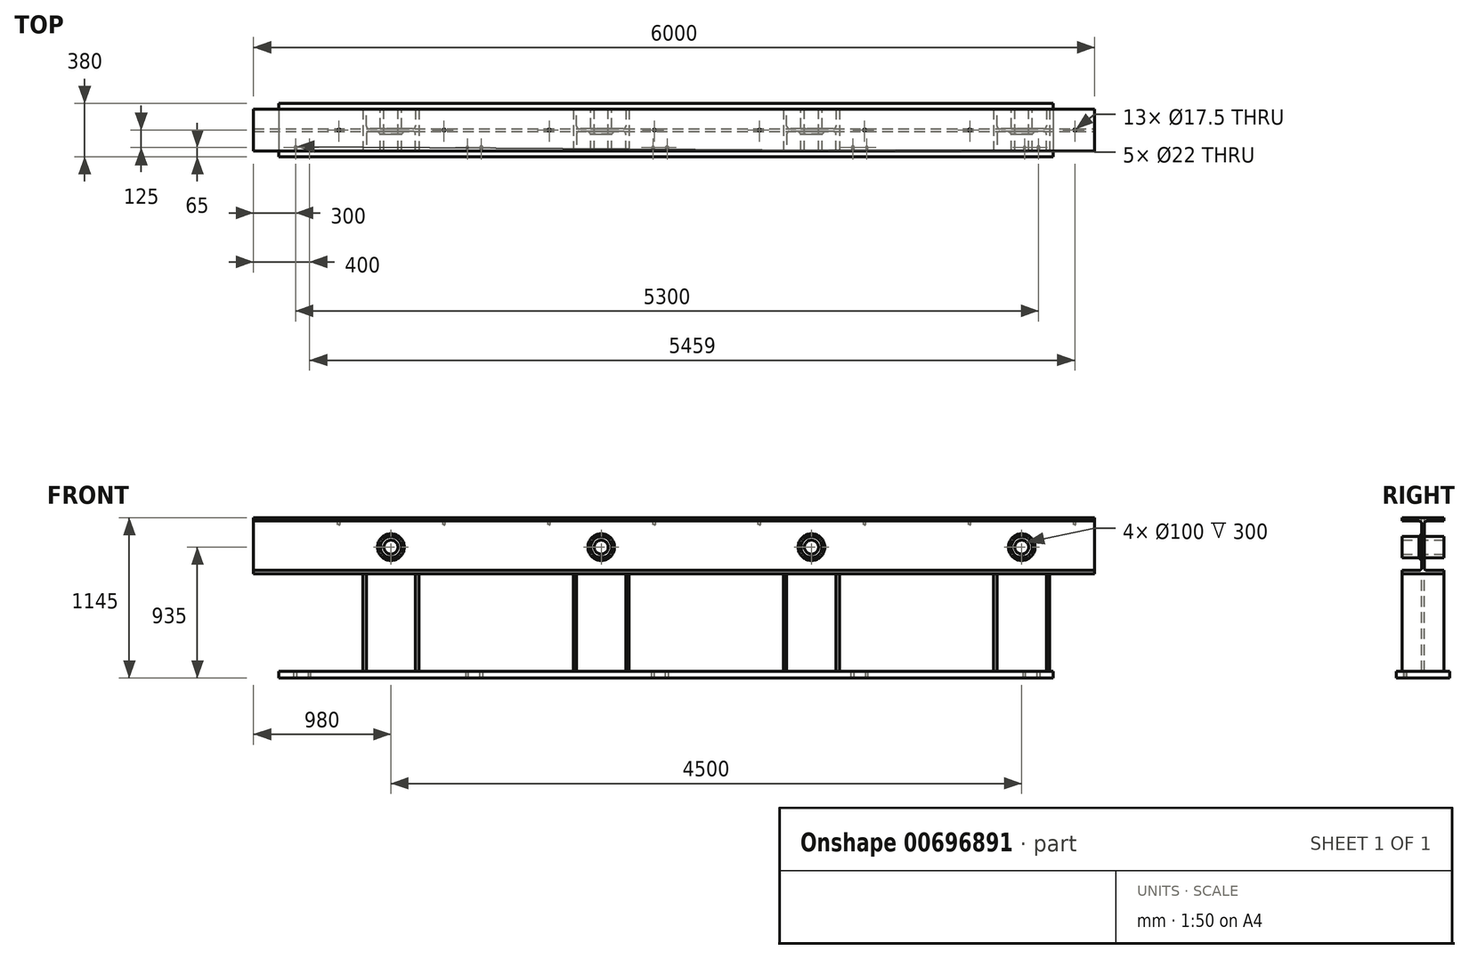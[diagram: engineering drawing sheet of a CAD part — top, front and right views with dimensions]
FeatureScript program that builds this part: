
annotation { "Feature Type Name" : "Feature", "Feature Type Description" : "" }
export const myFeature = defineFeature(function(context is Context, id is Id, definition is map)
    precondition{}
    {
        {
            var Q0;
            Q0=qCreatedBy(makeId("Right.planeOp"),FACE);
            var sketch = newSketch(context, id + "F0", { "sketchPlane" : qUnion([Q0])});
            skLineSegment(sketch, "E0", {"start": v(0, 400) * mm, "end": v(0, 0) * mm, "construction": true});
            skLineSegment(sketch, "E1", {"start": v(0, 0) * mm, "end": v(150, 0) * mm});
            skLineSegment(sketch, "E2", {"start": v(150, 0) * mm, "end": v(150, 24) * mm});
            skLineSegment(sketch, "E3", {"start": v(150, 24) * mm, "end": v(28.5, 24) * mm});
            skLineSegment(sketch, "E4", {"start": v(9.5, 43) * mm, "end": v(9.5, 357) * mm});
            skLineSegment(sketch, "E5", {"start": v(28.5, 376) * mm, "end": v(150, 376) * mm});
            skLineSegment(sketch, "E6", {"start": v(150, 376) * mm, "end": v(150, 400) * mm});
            skLineSegment(sketch, "E7", {"start": v(150, 400) * mm, "end": v(0, 400) * mm});
            skLineSegment(sketch, "E8.MirrorCS", {"start": v(-150, 0) * mm, "end": v(-150, 24) * mm});
            skLineSegment(sketch, "E9.MirrorCS", {"start": v(-150, 376) * mm, "end": v(-150, 400) * mm});
            skLineSegment(sketch, "E10.MirrorCS", {"start": v(-9.5, 43) * mm, "end": v(-9.5, 357) * mm});
            skLineSegment(sketch, "E11.MirrorCS", {"start": v(-150, 24) * mm, "end": v(-28.5, 24) * mm});
            skLineSegment(sketch, "E12.MirrorCS", {"start": v(-150, 400) * mm, "end": v(0, 400) * mm});
            skLineSegment(sketch, "E13.MirrorCS", {"start": v(0, 0) * mm, "end": v(-150, 0) * mm});
            skLineSegment(sketch, "E14.MirrorCS", {"start": v(-28.5, 376) * mm, "end": v(-150, 376) * mm});
            skPoint(sketch, "E15.visualSharp", {"position": v(9.5, 24) * mm});
            skArc(sketch, "E15.filletArc", {"start": v(9.5, 43) * mm, "mid": v(15.06, 29.56) * mm, "end": v(28.5, 24) * mm});
            skPoint(sketch, "E16.visualSharp", {"position": v(9.5, 376) * mm});
            skArc(sketch, "E16.filletArc", {"start": v(28.5, 376) * mm, "mid": v(15.06, 370.44) * mm, "end": v(9.5, 357) * mm});
            skPoint(sketch, "E17.visualSharp", {"position": v(-9.5, 376) * mm});
            skArc(sketch, "E17.filletArc", {"start": v(-9.5, 357) * mm, "mid": v(-15.06, 370.44) * mm, "end": v(-28.5, 376) * mm});
            skPoint(sketch, "E18.visualSharp", {"position": v(-9.5, 24) * mm});
            skArc(sketch, "E18.filletArc", {"start": v(-28.5, 24) * mm, "mid": v(-15.06, 29.56) * mm, "end": v(-9.5, 43) * mm});
            skSolve(sketch);
        }
        {
            var Q0;
            Q0 = qSketchRegion(id + "F0", true);
            extrude(context, id + "F1", {"entities" : qUnion([Q0]), "oppositeDirection" : true, "depth" : 6000 * mm, "offsetDistance" : 25 * mm});
        }
        {
            var Q0;
            Q0=qCreatedBy(makeId("Front.planeOp"),FACE);
            var sketch = newSketch(context, id + "F2", { "sketchPlane" : qUnion([Q0])});
            skCircle(sketch, "E19", {"center": v(-520, 190) * mm, "radius": 75 * mm});
            skCircle(sketch, "E20", {"center": v(-520, 190) * mm, "radius": 50 * mm});
            skCircle(sketch, "E21.1.0.0", {"center": v(-2020, 190) * mm, "radius": 75 * mm});
            skCircle(sketch, "E21.1.0.1", {"center": v(-2020, 190) * mm, "radius": 50 * mm});
            skCircle(sketch, "E21.2.0.0", {"center": v(-3520, 190) * mm, "radius": 75 * mm});
            skCircle(sketch, "E21.2.0.1", {"center": v(-3520, 190) * mm, "radius": 50 * mm});
            skCircle(sketch, "E21.3.0.0", {"center": v(-5020, 190) * mm, "radius": 75 * mm});
            skCircle(sketch, "E21.3.0.1", {"center": v(-5020, 190) * mm, "radius": 50 * mm});
            skLineSegment(sketch, "E21.direction1", {"start": v(-520, 190) * mm, "end": v(-2020, 190) * mm, "construction": true});
            skSolve(sketch);
        }
        {
            var Q0;
            Q0=makeQuery(id+"F2.imprint","IMPRINT",FACE,{"disambiguationData":[TD([[makeQuery(id+"F2.imprint","IMPRINT",EDGE,{"derivedFrom":sQuery(id+"F2.wireOp",EDGE,"E21.3.0.0")}),1.0]])]});
            var Q1;
            Q1=makeQuery(id+"F2.imprint","IMPRINT",FACE,{"disambiguationData":[TD([[makeQuery(id+"F2.imprint","IMPRINT",EDGE,{"derivedFrom":sQuery(id+"F2.wireOp",EDGE,"E21.3.0.1")}),1.0]])]});
            var Q2;
            Q2=makeQuery(id+"F2.imprint","IMPRINT",FACE,{"disambiguationData":[TD([[makeQuery(id+"F2.imprint","IMPRINT",EDGE,{"derivedFrom":sQuery(id+"F2.wireOp",EDGE,"E21.2.0.1")}),1.0]])]});
            var Q3;
            Q3=makeQuery(id+"F2.imprint","IMPRINT",FACE,{"disambiguationData":[TD([[makeQuery(id+"F2.imprint","IMPRINT",EDGE,{"derivedFrom":sQuery(id+"F2.wireOp",EDGE,"E21.2.0.0")}),1.0]])]});
            var Q4;
            Q4=makeQuery(id+"F2.imprint","IMPRINT",FACE,{"disambiguationData":[TD([[makeQuery(id+"F2.imprint","IMPRINT",EDGE,{"derivedFrom":sQuery(id+"F2.wireOp",EDGE,"E21.1.0.0")}),1.0]])]});
            var Q5;
            Q5=makeQuery(id+"F2.imprint","IMPRINT",FACE,{"disambiguationData":[TD([[makeQuery(id+"F2.imprint","IMPRINT",EDGE,{"derivedFrom":sQuery(id+"F2.wireOp",EDGE,"E21.1.0.1")}),1.0]])]});
            var Q6;
            Q6=makeQuery(id+"F2.imprint","IMPRINT",FACE,{"disambiguationData":[TD([[makeQuery(id+"F2.imprint","IMPRINT",EDGE,{"derivedFrom":sQuery(id+"F2.wireOp",EDGE,"E20")}),1.0]])]});
            var Q7;
            Q7=makeQuery(id+"F2.imprint","IMPRINT",FACE,{"disambiguationData":[TD([[makeQuery(id+"F2.imprint","IMPRINT",EDGE,{"derivedFrom":sQuery(id+"F2.wireOp",EDGE,"E19")}),1.0]])]});
            extrude(context, id + "F3", {"entities" : qUnion([Q0, Q1, Q2, Q3, Q4, Q5, Q6, Q7]), "operationType" : NewBodyOperationType.REMOVE, "endBound" : BoundingType.SYMMETRIC, "depth" : 50 * mm, "offsetDistance" : 25 * mm});
        }
        {
            var Q0;
            Q0 = qSketchRegion(id + "F2", true);
            extrude(context, id + "F4", {"entities" : qUnion([Q0]), "operationType" : NewBodyOperationType.ADD, "endBound" : BoundingType.SYMMETRIC, "depth" : 300 * mm, "offsetDistance" : 25 * mm});
        }
        {
            var Q0;
            Q0=qCreatedBy(makeId("Top.planeOp"),FACE);
            var sketch = newSketch(context, id + "F5", { "sketchPlane" : qUnion([Q0])});
            skLineSegment(sketch, "E22", {"start": v(-720, 0) * mm, "end": v(-320, 0) * mm, "construction": true});
            skLineSegment(sketch, "E23", {"start": v(-320, 0) * mm, "end": v(-320, 150) * mm});
            skLineSegment(sketch, "E24", {"start": v(-320, 150) * mm, "end": v(-344, 150) * mm});
            skLineSegment(sketch, "E25", {"start": v(-344, 150) * mm, "end": v(-344, 28.5) * mm});
            skLineSegment(sketch, "E26", {"start": v(-363, 9.5) * mm, "end": v(-677, 9.5) * mm});
            skLineSegment(sketch, "E27", {"start": v(-696, 28.5) * mm, "end": v(-696, 150) * mm});
            skLineSegment(sketch, "E28", {"start": v(-696, 150) * mm, "end": v(-720, 150) * mm});
            skLineSegment(sketch, "E29", {"start": v(-720, 150) * mm, "end": v(-720, 0) * mm});
            skPoint(sketch, "E30.visualSharp", {"position": v(-696, 9.5) * mm});
            skArc(sketch, "E30.filletArc", {"start": v(-696, 28.5) * mm, "mid": v(-690.44, 15.06) * mm, "end": v(-677, 9.5) * mm});
            skPoint(sketch, "E31.visualSharp", {"position": v(-344, 9.5) * mm});
            skArc(sketch, "E31.filletArc", {"start": v(-363, 9.5) * mm, "mid": v(-349.56, 15.06) * mm, "end": v(-344, 28.5) * mm});
            skArc(sketch, "E32.MirrorCS", {"start": v(-696, -28.5) * mm, "mid": v(-690.44, -15.06) * mm, "end": v(-677, -9.5) * mm});
            skArc(sketch, "E33.MirrorCS", {"start": v(-363, -9.5) * mm, "mid": v(-349.56, -15.06) * mm, "end": v(-344, -28.5) * mm});
            skLineSegment(sketch, "E34.MirrorCS", {"start": v(-720, -150) * mm, "end": v(-720, 0) * mm});
            skLineSegment(sketch, "E35.MirrorCS", {"start": v(-696, -150) * mm, "end": v(-720, -150) * mm});
            skLineSegment(sketch, "E36.MirrorCS", {"start": v(-696, -28.5) * mm, "end": v(-696, -150) * mm});
            skLineSegment(sketch, "E37.MirrorCS", {"start": v(-320, -150) * mm, "end": v(-344, -150) * mm});
            skLineSegment(sketch, "E38.MirrorCS", {"start": v(-344, -150) * mm, "end": v(-344, -28.5) * mm});
            skLineSegment(sketch, "E39.MirrorCS", {"start": v(-363, -9.5) * mm, "end": v(-677, -9.5) * mm});
            skPoint(sketch, "E40.MirrorP", {"position": v(-344, -9.5) * mm});
            skPoint(sketch, "E41.MirrorP", {"position": v(-696, -9.5) * mm});
            skLineSegment(sketch, "E42.MirrorCS", {"start": v(-320, 0) * mm, "end": v(-320, -150) * mm});
            skLineSegment(sketch, "E43.1.0.0", {"start": v(-1820, 0) * mm, "end": v(-1820, -150) * mm});
            skPoint(sketch, "E43.1.0.1", {"position": v(-2196, -9.5) * mm});
            skLineSegment(sketch, "E43.1.0.2", {"start": v(-1844, -150) * mm, "end": v(-1844, -28.5) * mm});
            skLineSegment(sketch, "E43.1.0.3", {"start": v(-2196, -28.5) * mm, "end": v(-2196, -150) * mm});
            skLineSegment(sketch, "E43.1.0.4", {"start": v(-2220, 0) * mm, "end": v(-1820, 0) * mm, "construction": true});
            skLineSegment(sketch, "E43.1.0.5", {"start": v(-1820, 0) * mm, "end": v(-1820, 150) * mm});
            skLineSegment(sketch, "E43.1.0.6", {"start": v(-1844, 150) * mm, "end": v(-1844, 28.5) * mm});
            skLineSegment(sketch, "E43.1.0.7", {"start": v(-1863, 9.5) * mm, "end": v(-2177, 9.5) * mm});
            skLineSegment(sketch, "E43.1.0.8", {"start": v(-2196, 28.5) * mm, "end": v(-2196, 150) * mm});
            skLineSegment(sketch, "E43.1.0.9", {"start": v(-2220, 150) * mm, "end": v(-2220, 0) * mm});
            skLineSegment(sketch, "E43.1.0.10", {"start": v(-2220, -150) * mm, "end": v(-2220, 0) * mm});
            skPoint(sketch, "E43.1.0.11", {"position": v(-1844, -9.5) * mm});
            skLineSegment(sketch, "E43.1.0.12", {"start": v(-1863, -9.5) * mm, "end": v(-2177, -9.5) * mm});
            skPoint(sketch, "E43.1.0.13", {"position": v(-1844, 9.5) * mm});
            skPoint(sketch, "E43.1.0.14", {"position": v(-2196, 9.5) * mm});
            skLineSegment(sketch, "E43.1.0.15", {"start": v(-2196, -150) * mm, "end": v(-2220, -150) * mm});
            skLineSegment(sketch, "E43.1.0.16", {"start": v(-1820, -150) * mm, "end": v(-1844, -150) * mm});
            skLineSegment(sketch, "E43.1.0.17", {"start": v(-1820, 150) * mm, "end": v(-1844, 150) * mm});
            skLineSegment(sketch, "E43.1.0.18", {"start": v(-2196, 150) * mm, "end": v(-2220, 150) * mm});
            skArc(sketch, "E43.1.0.19", {"start": v(-2196, 28.5) * mm, "mid": v(-2190.44, 15.06) * mm, "end": v(-2177, 9.5) * mm});
            skArc(sketch, "E43.1.0.20", {"start": v(-1863, 9.5) * mm, "mid": v(-1849.56, 15.06) * mm, "end": v(-1844, 28.5) * mm});
            skArc(sketch, "E43.1.0.21", {"start": v(-2196, -28.5) * mm, "mid": v(-2190.44, -15.06) * mm, "end": v(-2177, -9.5) * mm});
            skArc(sketch, "E43.1.0.22", {"start": v(-1863, -9.5) * mm, "mid": v(-1849.56, -15.06) * mm, "end": v(-1844, -28.5) * mm});
            skLineSegment(sketch, "E43.2.0.0", {"start": v(-3320, 0) * mm, "end": v(-3320, -150) * mm});
            skPoint(sketch, "E43.2.0.1", {"position": v(-3696, -9.5) * mm});
            skLineSegment(sketch, "E43.2.0.2", {"start": v(-3344, -150) * mm, "end": v(-3344, -28.5) * mm});
            skLineSegment(sketch, "E43.2.0.3", {"start": v(-3696, -28.5) * mm, "end": v(-3696, -150) * mm});
            skLineSegment(sketch, "E43.2.0.4", {"start": v(-3720, 0) * mm, "end": v(-3320, 0) * mm, "construction": true});
            skLineSegment(sketch, "E43.2.0.5", {"start": v(-3320, 0) * mm, "end": v(-3320, 150) * mm});
            skLineSegment(sketch, "E43.2.0.6", {"start": v(-3344, 150) * mm, "end": v(-3344, 28.5) * mm});
            skLineSegment(sketch, "E43.2.0.7", {"start": v(-3363, 9.5) * mm, "end": v(-3677, 9.5) * mm});
            skLineSegment(sketch, "E43.2.0.8", {"start": v(-3696, 28.5) * mm, "end": v(-3696, 150) * mm});
            skLineSegment(sketch, "E43.2.0.9", {"start": v(-3720, 150) * mm, "end": v(-3720, 0) * mm});
            skLineSegment(sketch, "E43.2.0.10", {"start": v(-3720, -150) * mm, "end": v(-3720, 0) * mm});
            skPoint(sketch, "E43.2.0.11", {"position": v(-3344, -9.5) * mm});
            skLineSegment(sketch, "E43.2.0.12", {"start": v(-3363, -9.5) * mm, "end": v(-3677, -9.5) * mm});
            skPoint(sketch, "E43.2.0.13", {"position": v(-3344, 9.5) * mm});
            skPoint(sketch, "E43.2.0.14", {"position": v(-3696, 9.5) * mm});
            skLineSegment(sketch, "E43.2.0.15", {"start": v(-3696, -150) * mm, "end": v(-3720, -150) * mm});
            skLineSegment(sketch, "E43.2.0.16", {"start": v(-3320, -150) * mm, "end": v(-3344, -150) * mm});
            skLineSegment(sketch, "E43.2.0.17", {"start": v(-3320, 150) * mm, "end": v(-3344, 150) * mm});
            skLineSegment(sketch, "E43.2.0.18", {"start": v(-3696, 150) * mm, "end": v(-3720, 150) * mm});
            skArc(sketch, "E43.2.0.19", {"start": v(-3696, 28.5) * mm, "mid": v(-3690.44, 15.06) * mm, "end": v(-3677, 9.5) * mm});
            skArc(sketch, "E43.2.0.20", {"start": v(-3363, 9.5) * mm, "mid": v(-3349.56, 15.06) * mm, "end": v(-3344, 28.5) * mm});
            skArc(sketch, "E43.2.0.21", {"start": v(-3696, -28.5) * mm, "mid": v(-3690.44, -15.06) * mm, "end": v(-3677, -9.5) * mm});
            skArc(sketch, "E43.2.0.22", {"start": v(-3363, -9.5) * mm, "mid": v(-3349.56, -15.06) * mm, "end": v(-3344, -28.5) * mm});
            skLineSegment(sketch, "E43.direction1", {"start": v(-2220, -150) * mm, "end": v(-720, -150) * mm, "construction": true});
            skLineSegment(sketch, "E44.0.3.0", {"start": v(-4820, 0) * mm, "end": v(-4820, -150) * mm});
            skPoint(sketch, "E44.3.3.0", {"position": v(-5196, -9.5) * mm});
            skLineSegment(sketch, "E44.4.3.0", {"start": v(-4844, -150) * mm, "end": v(-4844, -28.5) * mm});
            skLineSegment(sketch, "E44.7.3.0", {"start": v(-5196, -28.5) * mm, "end": v(-5196, -150) * mm});
            skLineSegment(sketch, "E44.10.3.0", {"start": v(-5220, 0) * mm, "end": v(-4820, 0) * mm, "construction": true});
            skLineSegment(sketch, "E44.13.3.0", {"start": v(-4820, 0) * mm, "end": v(-4820, 150) * mm});
            skLineSegment(sketch, "E44.16.3.0", {"start": v(-4844, 150) * mm, "end": v(-4844, 28.5) * mm});
            skLineSegment(sketch, "E44.19.3.0", {"start": v(-4863, 9.5) * mm, "end": v(-5177, 9.5) * mm});
            skLineSegment(sketch, "E44.22.3.0", {"start": v(-5196, 28.5) * mm, "end": v(-5196, 150) * mm});
            skLineSegment(sketch, "E44.25.3.0", {"start": v(-5220, 150) * mm, "end": v(-5220, 0) * mm});
            skLineSegment(sketch, "E44.28.3.0", {"start": v(-5220, -150) * mm, "end": v(-5220, 0) * mm});
            skPoint(sketch, "E44.31.3.0", {"position": v(-4844, -9.5) * mm});
            skLineSegment(sketch, "E44.32.3.0", {"start": v(-4863, -9.5) * mm, "end": v(-5177, -9.5) * mm});
            skPoint(sketch, "E44.35.3.0", {"position": v(-4844, 9.5) * mm});
            skPoint(sketch, "E44.36.3.0", {"position": v(-5196, 9.5) * mm});
            skLineSegment(sketch, "E44.37.3.0", {"start": v(-5196, -150) * mm, "end": v(-5220, -150) * mm});
            skLineSegment(sketch, "E44.40.3.0", {"start": v(-4820, -150) * mm, "end": v(-4844, -150) * mm});
            skLineSegment(sketch, "E44.43.3.0", {"start": v(-4820, 150) * mm, "end": v(-4844, 150) * mm});
            skLineSegment(sketch, "E44.46.3.0", {"start": v(-5196, 150) * mm, "end": v(-5220, 150) * mm});
            skArc(sketch, "E44.49.3.0", {"start": v(-5196, 28.5) * mm, "mid": v(-5190.44, 15.06) * mm, "end": v(-5177, 9.5) * mm});
            skArc(sketch, "E44.53.3.0", {"start": v(-4863, 9.5) * mm, "mid": v(-4849.56, 15.06) * mm, "end": v(-4844, 28.5) * mm});
            skArc(sketch, "E44.57.3.0", {"start": v(-5196, -28.5) * mm, "mid": v(-5190.44, -15.06) * mm, "end": v(-5177, -9.5) * mm});
            skArc(sketch, "E44.61.3.0", {"start": v(-4863, -9.5) * mm, "mid": v(-4849.56, -15.06) * mm, "end": v(-4844, -28.5) * mm});
            skSolve(sketch);
        }
        {
            var Q0;
            Q0=makeQuery(id+"F5.imprint","IMPRINT",FACE,{"disambiguationData":[TD([[makeQuery(id+"F5.imprint","IMPRINT",EDGE,{"derivedFrom":sQuery(id+"F5.wireOp",EDGE,"E23")}),1.0]])]});
            var Q1;
            Q1=makeQuery(id+"F5.imprint","IMPRINT",FACE,{"disambiguationData":[TD([[makeQuery(id+"F5.imprint","IMPRINT",EDGE,{"derivedFrom":sQuery(id+"F5.wireOp",EDGE,"E43.1.0.0")}),-1.0]])]});
            var Q2;
            Q2=makeQuery(id+"F5.imprint","IMPRINT",FACE,{"disambiguationData":[TD([[makeQuery(id+"F5.imprint","IMPRINT",EDGE,{"derivedFrom":sQuery(id+"F5.wireOp",EDGE,"E43.2.0.0")}),-1.0]])]});
            var Q3;
            Q3=makeQuery(id+"F5.imprint","IMPRINT",FACE,{"disambiguationData":[TD([[makeQuery(id+"F5.imprint","IMPRINT",EDGE,{"derivedFrom":sQuery(id+"F5.wireOp",EDGE,"E44.0.3.0")}),-1.0]])]});
            extrude(context, id + "F6", {"entities" : qUnion([Q0, Q1, Q2, Q3]), "depth" : -695 * mm, "offsetDistance" : 25 * mm});
        }
        {
            var Q0;
            Q0=makeQuery(id+"F6.opExtrude","CAP_FACE",FACE,{"disambiguationData":[OSD([sQuery(id+"F5.wireOp",EDGE,"E43.2.0.0"),sQuery(id+"F5.wireOp",EDGE,"E43.2.0.2"),sQuery(id+"F5.wireOp",EDGE,"E43.2.0.3"),sQuery(id+"F5.wireOp",EDGE,"E43.2.0.5"),sQuery(id+"F5.wireOp",EDGE,"E43.2.0.6"),sQuery(id+"F5.wireOp",EDGE,"E43.2.0.7"),sQuery(id+"F5.wireOp",EDGE,"E43.2.0.8"),sQuery(id+"F5.wireOp",EDGE,"E43.2.0.9"),sQuery(id+"F5.wireOp",EDGE,"E43.2.0.10"),sQuery(id+"F5.wireOp",EDGE,"E43.2.0.12"),sQuery(id+"F5.wireOp",EDGE,"E43.2.0.15"),sQuery(id+"F5.wireOp",EDGE,"E43.2.0.16"),sQuery(id+"F5.wireOp",EDGE,"E43.2.0.17"),sQuery(id+"F5.wireOp",EDGE,"E43.2.0.18"),sQuery(id+"F5.wireOp",EDGE,"E43.2.0.19"),sQuery(id+"F5.wireOp",EDGE,"E43.2.0.20"),sQuery(id+"F5.wireOp",EDGE,"E43.2.0.21"),sQuery(id+"F5.wireOp",EDGE,"E43.2.0.22")])],"isStart":false});
            var sketch = newSketch(context, id + "F7", { "sketchPlane" : qUnion([Q0])});
            skLineSegment(sketch, "E45.bottom", {"start": v(-5820, -190) * mm, "end": v(-295, -190) * mm});
            skLineSegment(sketch, "E45.top", {"start": v(-5820, 190) * mm, "end": v(-295, 190) * mm});
            skLineSegment(sketch, "E45.left", {"start": v(-5820, -190) * mm, "end": v(-5820, 190) * mm});
            skLineSegment(sketch, "E45.right", {"start": v(-295, -190) * mm, "end": v(-295, 190) * mm});
            skSolve(sketch);
        }
        {
            var Q0;
            Q0 = qSketchRegion(id + "F7", true);
            extrude(context, id + "F8", {"entities" : qUnion([Q0]), "depth" : 50 * mm, "offsetDistance" : 25 * mm});
        }
        {
            var Q0;
            Q0=makeQuery(id+"F3.boolean.opBoolean","INTERSECT",EDGE,{"derivedFrom":[makeQuery(id+"F1.opExtrude","SWEPT_FACE",FACE,{"disambiguationData":[OSD([sQuery(id+"F0.wireOp",EDGE,"E10.MirrorCS")])]}),makeQuery(id+"F3.opExtrude","SWEPT_FACE",FACE,{"disambiguationData":[OSD([sQuery(id+"F2.wireOp",EDGE,"E21.3.0.0")])]})]});
            var Q1;
            Q1=makeQuery(id+"F3.boolean.opBoolean","INTERSECT",EDGE,{"derivedFrom":[makeQuery(id+"F1.opExtrude","SWEPT_FACE",FACE,{"disambiguationData":[OSD([sQuery(id+"F0.wireOp",EDGE,"E10.MirrorCS")])]}),makeQuery(id+"F3.opExtrude","SWEPT_FACE",FACE,{"disambiguationData":[OSD([sQuery(id+"F2.wireOp",EDGE,"E21.2.0.0")])]})]});
            var Q2;
            Q2=makeQuery(id+"F3.boolean.opBoolean","INTERSECT",EDGE,{"derivedFrom":[makeQuery(id+"F1.opExtrude","SWEPT_FACE",FACE,{"disambiguationData":[OSD([sQuery(id+"F0.wireOp",EDGE,"E10.MirrorCS")])]}),makeQuery(id+"F3.opExtrude","SWEPT_FACE",FACE,{"disambiguationData":[OSD([sQuery(id+"F2.wireOp",EDGE,"E21.1.0.0")])]})]});
            var Q3;
            Q3=makeQuery(id+"F3.boolean.opBoolean","INTERSECT",EDGE,{"derivedFrom":[makeQuery(id+"F1.opExtrude","SWEPT_FACE",FACE,{"disambiguationData":[OSD([sQuery(id+"F0.wireOp",EDGE,"E10.MirrorCS")])]}),makeQuery(id+"F3.opExtrude","SWEPT_FACE",FACE,{"disambiguationData":[OSD([sQuery(id+"F2.wireOp",EDGE,"E19")])]})]});
            var Q4;
            Q4=makeQuery(id+"F3.boolean.opBoolean","INTERSECT",EDGE,{"derivedFrom":[makeQuery(id+"F1.opExtrude","SWEPT_FACE",FACE,{"disambiguationData":[OSD([sQuery(id+"F0.wireOp",EDGE,"E4")])]}),makeQuery(id+"F3.opExtrude","SWEPT_FACE",FACE,{"disambiguationData":[OSD([sQuery(id+"F2.wireOp",EDGE,"E19")])]})]});
            var Q5;
            Q5=makeQuery(id+"F3.boolean.opBoolean","INTERSECT",EDGE,{"derivedFrom":[makeQuery(id+"F1.opExtrude","SWEPT_FACE",FACE,{"disambiguationData":[OSD([sQuery(id+"F0.wireOp",EDGE,"E4")])]}),makeQuery(id+"F3.opExtrude","SWEPT_FACE",FACE,{"disambiguationData":[OSD([sQuery(id+"F2.wireOp",EDGE,"E21.1.0.0")])]})]});
            var Q6;
            Q6=makeQuery(id+"F3.boolean.opBoolean","INTERSECT",EDGE,{"derivedFrom":[makeQuery(id+"F1.opExtrude","SWEPT_FACE",FACE,{"disambiguationData":[OSD([sQuery(id+"F0.wireOp",EDGE,"E4")])]}),makeQuery(id+"F3.opExtrude","SWEPT_FACE",FACE,{"disambiguationData":[OSD([sQuery(id+"F2.wireOp",EDGE,"E21.2.0.0")])]})]});
            var Q7;
            Q7=makeQuery(id+"F3.boolean.opBoolean","INTERSECT",EDGE,{"derivedFrom":[makeQuery(id+"F1.opExtrude","SWEPT_FACE",FACE,{"disambiguationData":[OSD([sQuery(id+"F0.wireOp",EDGE,"E4")])]}),makeQuery(id+"F3.opExtrude","SWEPT_FACE",FACE,{"disambiguationData":[OSD([sQuery(id+"F2.wireOp",EDGE,"E21.3.0.0")])]})]});
            chamfer(context, id + "F9", {"entities" : qUnion([Q0, Q1, Q2, Q3, Q4, Q5, Q6, Q7]), "width" : 20 * mm, "tangentPropagation" : true});
        }
        {
            var Q0;
            Q0=makeQuery(id+"F1.opExtrude","SWEPT_FACE",FACE,{"disambiguationData":[OSD([sQuery(id+"F0.wireOp",EDGE,"E7"),sQuery(id+"F0.wireOp",EDGE,"E12.MirrorCS")])]});
            var sketch = newSketch(context, id + "F10", { "sketchPlane" : qUnion([Q0])});
            skPoint(sketch, "E46", {"position": v(-141, 0) * mm});
            skPoint(sketch, "E47.1.0.0", {"position": v(-891, 0) * mm});
            skPoint(sketch, "E47.2.0.0", {"position": v(-1641, 0) * mm});
            skPoint(sketch, "E47.3.0.0", {"position": v(-2391, 0) * mm});
            skPoint(sketch, "E47.4.0.0", {"position": v(-3141, 0) * mm});
            skPoint(sketch, "E47.5.0.0", {"position": v(-3891, 0) * mm});
            skPoint(sketch, "E47.6.0.0", {"position": v(-4641, 0) * mm});
            skPoint(sketch, "E47.7.0.0", {"position": v(-5391, 0) * mm});
            skLineSegment(sketch, "E47.direction1", {"start": v(-141, 0) * mm, "end": v(-891, 0) * mm, "construction": true});
            skSolve(sketch);
        }
        {
            var Q0;
            Q0=sQuery(id+"F10.wireOp",VERTEX,"E46");
            var Q1;
            Q1=sQuery(id+"F10.wireOp",VERTEX,"E47.1.0.0");
            var Q2;
            Q2=sQuery(id+"F10.wireOp",VERTEX,"E47.2.0.0");
            var Q3;
            Q3=sQuery(id+"F10.wireOp",VERTEX,"E47.3.0.0");
            var Q4;
            Q4=sQuery(id+"F10.wireOp",VERTEX,"E47.4.0.0");
            var Q5;
            Q5=sQuery(id+"F10.wireOp",VERTEX,"E47.5.0.0");
            var Q6;
            Q6=sQuery(id+"F10.wireOp",VERTEX,"E47.6.0.0");
            var Q7;
            Q7=sQuery(id+"F10.wireOp",VERTEX,"E47.7.0.0");
            var Q8;
            Q8=makeQuery(id+"F1.opExtrude","SWEPT_BODY",BODY,{"disambiguationData":[OSD([sQuery(id+"F0.wireOp",EDGE,"E1"),sQuery(id+"F0.wireOp",EDGE,"E2"),sQuery(id+"F0.wireOp",EDGE,"E3"),sQuery(id+"F0.wireOp",EDGE,"E4"),sQuery(id+"F0.wireOp",EDGE,"E5"),sQuery(id+"F0.wireOp",EDGE,"E6"),sQuery(id+"F0.wireOp",EDGE,"E7"),sQuery(id+"F0.wireOp",EDGE,"E8.MirrorCS"),sQuery(id+"F0.wireOp",EDGE,"E9.MirrorCS"),sQuery(id+"F0.wireOp",EDGE,"E10.MirrorCS"),sQuery(id+"F0.wireOp",EDGE,"E11.MirrorCS"),sQuery(id+"F0.wireOp",EDGE,"E12.MirrorCS"),sQuery(id+"F0.wireOp",EDGE,"E13.MirrorCS"),sQuery(id+"F0.wireOp",EDGE,"E14.MirrorCS"),sQuery(id+"F0.wireOp",EDGE,"E15.filletArc"),sQuery(id+"F0.wireOp",EDGE,"E16.filletArc"),sQuery(id+"F0.wireOp",EDGE,"E17.filletArc"),sQuery(id+"F0.wireOp",EDGE,"E18.filletArc")])]});
            hole(context, id + "F11", {"style" : HoleStyle.SIMPLE, "endStyle" : HoleEndStyle.BLIND, "standardTappedOrClearance" : lookupTablePath({ "standard" : "ISO", "engagement" : "75%", "pitch" : "2.5 mm", "size" : "M20", "type" : "Tapped" }), "standardBlindInLast" : lookupTablePath({ "standard" : "ISO", "engagement" : "75%", "pitch" : "2.5 mm", "size" : "M20", "type" : "Tapped" }), "holeDiameter" : 17.5 * mm, "majorDiameter" : 20 * mm, "showTappedDepth" : true, "holeDepth" : 47.5 * mm, "isTappedThrough" : true, "tappedDepth" : 35 * mm, "tapClearance" : 5, "startFromSketch" : true, "locations" : qUnion([Q0, Q1, Q2, Q3, Q4, Q5, Q6, Q7]), "scope" : qUnion([Q8])});
        }
        {
            var Q0;
            Q0=makeQuery(id+"F7.imprint","IMPRINT",FACE,{"disambiguationData":[TD([[makeQuery(id+"F7.imprint","IMPRINT",EDGE,{"derivedFrom":sQuery(id+"F7.wireOp",EDGE,"E45.bottom")}),1.0]])]});
            var sketch = newSketch(context, id + "F12", { "sketchPlane" : qUnion([Q0])});
            skPoint(sketch, "E48", {"position": v(-400, 125) * mm});
            skPoint(sketch, "E49", {"position": v(-500, 125) * mm});
            skPoint(sketch, "E50", {"position": v(-1625, 125) * mm});
            skPoint(sketch, "E51", {"position": v(-1725, 125) * mm});
            skPoint(sketch, "E52", {"position": v(-3050, 125) * mm});
            skPoint(sketch, "E53", {"position": v(-3150, 125) * mm});
            skPoint(sketch, "E54", {"position": v(-4375, 125) * mm});
            skPoint(sketch, "E55", {"position": v(-4475, 125) * mm});
            skPoint(sketch, "E56", {"position": v(-5600, 125) * mm});
            skPoint(sketch, "E57", {"position": v(-5700, 125) * mm});
            skSolve(sketch);
        }
        {
            var Q0;
            Q0=sQuery(id+"F12.wireOp",VERTEX,"E48");
            var Q1;
            Q1=sQuery(id+"F12.wireOp",VERTEX,"E51");
            var Q2;
            Q2=sQuery(id+"F12.wireOp",VERTEX,"E52");
            var Q3;
            Q3=sQuery(id+"F12.wireOp",VERTEX,"E54");
            var Q4;
            Q4=sQuery(id+"F12.wireOp",VERTEX,"E57");
            var Q5;
            Q5=makeQuery(id+"F8.opExtrude","SWEPT_BODY",BODY,{"disambiguationData":[OSD([sQuery(id+"F7.wireOp",EDGE,"E45.bottom"),sQuery(id+"F7.wireOp",EDGE,"E45.top"),sQuery(id+"F7.wireOp",EDGE,"E45.left"),sQuery(id+"F7.wireOp",EDGE,"E45.right")])]});
            hole(context, id + "F13", {"style" : HoleStyle.SIMPLE, "endStyle" : HoleEndStyle.THROUGH, "oppositeDirection" : true, "standardTappedOrClearance" : lookupTablePath({ "standard" : "ISO", "fit" : "Normal", "size" : "M20", "type" : "Clearance" }), "standardBlindInLast" : lookupTablePath({ "fit" : "Standard", "standard" : "ISO", "size" : "M20", "type" : "Clearance" }), "holeDiameter" : 22 * mm, "majorDiameter" : 5 * mm, "isTappedThrough" : true, "tappedDepth" : 35 * mm, "tapClearance" : 5, "startFromSketch" : true, "locations" : qUnion([Q0, Q1, Q2, Q3, Q4]), "scope" : qUnion([Q5])});
        }
        {
            var Q0;
            Q0=sQuery(id+"F12.wireOp",VERTEX,"E49");
            var Q1;
            Q1=sQuery(id+"F12.wireOp",VERTEX,"E50");
            var Q2;
            Q2=sQuery(id+"F12.wireOp",VERTEX,"E53");
            var Q3;
            Q3=sQuery(id+"F12.wireOp",VERTEX,"E55");
            var Q4;
            Q4=sQuery(id+"F12.wireOp",VERTEX,"E56");
            var Q5;
            Q5=makeQuery(id+"F8.opExtrude","SWEPT_BODY",BODY,{"disambiguationData":[OSD([sQuery(id+"F7.wireOp",EDGE,"E45.bottom"),sQuery(id+"F7.wireOp",EDGE,"E45.top"),sQuery(id+"F7.wireOp",EDGE,"E45.left"),sQuery(id+"F7.wireOp",EDGE,"E45.right")])]});
            hole(context, id + "F14", {"style" : HoleStyle.SIMPLE, "endStyle" : HoleEndStyle.THROUGH, "oppositeDirection" : true, "standardTappedOrClearance" : lookupTablePath({ "standard" : "ISO", "engagement" : "75%", "pitch" : "2.5 mm", "size" : "M20", "type" : "Tapped" }), "standardBlindInLast" : lookupTablePath({ "standard" : "ISO", "engagement" : "75%", "pitch" : "2.5 mm", "size" : "M20", "type" : "Tapped" }), "holeDiameter" : 17.5 * mm, "majorDiameter" : 20 * mm, "showTappedDepth" : true, "isTappedThrough" : true, "tappedDepth" : 50 * mm, "tapClearance" : 5, "startFromSketch" : true, "locations" : qUnion([Q0, Q1, Q2, Q3, Q4]), "scope" : qUnion([Q5])});
        }
    });
